annotation { "Feature Type Name" : "Feature", "Feature Type Description" : "" }
export const myFeature = defineFeature(function(context is Context, id is Id, definition is map)
    precondition{}
    {
        {
            var Q0;
            Q0=qCreatedBy(makeId("Right.planeOp"),FACE);
            var sketch = newSketch(context, id + "F0", { "sketchPlane" : qUnion([Q0])});
            skLineSegment(sketch, "E0", {"start": v(0, 0) * mm, "end": v(-381, 0) * mm});
            skLineSegment(sketch, "E1", {"start": v(0, 0) * mm, "end": v(381, 0) * mm});
            skLineSegment(sketch, "E2", {"start": v(0, 0) * mm, "end": v(0, 190.5) * mm});
            skLineSegment(sketch, "E3", {"start": v(-381, 0) * mm, "end": v(0, 190.5) * mm});
            skLineSegment(sketch, "E4", {"start": v(0, 190.5) * mm, "end": v(381, 0) * mm});
            skLineSegment(sketch, "E5", {"start": v(381, 0) * mm, "end": v(457.2, 0) * mm});
            skLineSegment(sketch, "E6", {"start": v(0, 190.5) * mm, "end": v(0, 228.6) * mm});
            skLineSegment(sketch, "E7", {"start": v(-381, 0) * mm, "end": v(-457.2, 0) * mm});
            skLineSegment(sketch, "E8", {"start": v(-457.2, 0) * mm, "end": v(0, 228.6) * mm});
            skLineSegment(sketch, "E9", {"start": v(0, 228.6) * mm, "end": v(457.2, 0) * mm});
            skLineSegment(sketch, "E10", {"start": v(-381, 0) * mm, "end": v(-381, -279.4) * mm});
            skLineSegment(sketch, "E11", {"start": v(381, 0) * mm, "end": v(381, -279.4) * mm});
            skLineSegment(sketch, "E12", {"start": v(-381, -279.4) * mm, "end": v(381, -279.4) * mm});
            skLineSegment(sketch, "E13", {"start": v(-381, -279.4) * mm, "end": v(-381, -330.2) * mm});
            skLineSegment(sketch, "E14", {"start": v(381, -279.4) * mm, "end": v(381, -330.2) * mm});
            skLineSegment(sketch, "E15", {"start": v(-381, -330.2) * mm, "end": v(381, -330.2) * mm});
            skLineSegment(sketch, "E16", {"start": v(381, -279.4) * mm, "end": v(762, -279.4) * mm});
            skLineSegment(sketch, "E17", {"start": v(381, -330.2) * mm, "end": v(762, -330.2) * mm});
            skLineSegment(sketch, "E18", {"start": v(762, -279.4) * mm, "end": v(762, -330.2) * mm});
            skLineSegment(sketch, "E19", {"start": v(762, -279.4) * mm, "end": v(762, -50.8) * mm});
            skLineSegment(sketch, "E20", {"start": v(381, 0) * mm, "end": v(762, -50.8) * mm});
            skLineSegment(sketch, "E21", {"start": v(762, -50.8) * mm, "end": v(762, -101.6) * mm});
            skLineSegment(sketch, "E22", {"start": v(762, -101.6) * mm, "end": v(381, -50.8) * mm});
            skLineSegment(sketch, "E23", {"start": v(-279.4, -279.4) * mm, "end": v(-279.4, -101.6) * mm});
            skLineSegment(sketch, "E24", {"start": v(-279.4, -101.6) * mm, "end": v(-203.2, -101.6) * mm});
            skLineSegment(sketch, "E25", {"start": v(-203.2, -101.6) * mm, "end": v(-203.2, -279.4) * mm});
            skLineSegment(sketch, "E26", {"start": v(-203.2, -279.4) * mm, "end": v(-279.4, -279.4) * mm});
            skLineSegment(sketch, "E27.0", {"start": v(-177.8, -76.2) * mm, "end": v(-177.8, -279.4) * mm});
            skLineSegment(sketch, "E27.1", {"start": v(-304.8, -76.2) * mm, "end": v(-177.8, -76.2) * mm});
            skLineSegment(sketch, "E27.2", {"start": v(-304.8, -279.4) * mm, "end": v(-304.8, -76.2) * mm});
            skLineSegment(sketch, "E28", {"start": v(279.4, -88.9) * mm, "end": v(279.4, -203.2) * mm});
            skLineSegment(sketch, "E29", {"start": v(279.4, -88.9) * mm, "end": v(50.8, -88.9) * mm});
            skLineSegment(sketch, "E30", {"start": v(50.8, -88.9) * mm, "end": v(50.8, -203.2) * mm});
            skLineSegment(sketch, "E31", {"start": v(50.8, -203.2) * mm, "end": v(279.4, -203.2) * mm});
            skLineSegment(sketch, "E32.0", {"start": v(63.5, -101.6) * mm, "end": v(63.5, -190.5) * mm});
            skLineSegment(sketch, "E32.1", {"start": v(266.7, -101.6) * mm, "end": v(63.5, -101.6) * mm});
            skLineSegment(sketch, "E32.2", {"start": v(266.7, -101.6) * mm, "end": v(266.7, -190.5) * mm});
            skLineSegment(sketch, "E32.3", {"start": v(63.5, -190.5) * mm, "end": v(266.7, -190.5) * mm});
            skLineSegment(sketch, "E33.bottom", {"start": v(508, -118.98) * mm, "end": v(609.6, -118.98) * mm});
            skLineSegment(sketch, "E33.top", {"start": v(508, -220.58) * mm, "end": v(609.6, -220.58) * mm});
            skLineSegment(sketch, "E33.left", {"start": v(508, -118.98) * mm, "end": v(508, -220.58) * mm});
            skLineSegment(sketch, "E33.right", {"start": v(609.6, -118.98) * mm, "end": v(609.6, -220.58) * mm});
            skLineSegment(sketch, "E34.0", {"start": v(490.22, -238.36) * mm, "end": v(627.38, -238.36) * mm});
            skLineSegment(sketch, "E34.1", {"start": v(490.22, -101.2) * mm, "end": v(490.22, -238.36) * mm});
            skLineSegment(sketch, "E34.2", {"start": v(490.22, -101.2) * mm, "end": v(627.38, -101.2) * mm});
            skLineSegment(sketch, "E34.3", {"start": v(627.38, -101.2) * mm, "end": v(627.38, -238.36) * mm});
            skSolve(sketch);
        }
        {
            var Q0;
            Q0=makeQuery(id+"F0.imprint","IMPRINT",FACE,{"disambiguationData":[TD([[makeQuery(id+"F0.imprint","IMPRINT",EDGE,{"derivedFrom":sQuery(id+"F0.wireOp",EDGE,"E0")}),1.0]])]});
            var Q1;
            {var subQ5=sQuery(id+"F0.wireOp",EDGE,"E13");Q1=makeQuery(id+"F0.imprint","IMPRINT",FACE,{"disambiguationData":[TD([[makeQuery(id+"F0.imprint","IMPRINT",EDGE,{"derivedFrom":subQ5}),1.0]])]});}
            var Q2;
            Q2=makeQuery(id+"F0.imprint","IMPRINT",FACE,{"disambiguationData":[TD([[makeQuery(id+"F0.imprint","IMPRINT",EDGE,{"derivedFrom":sQuery(id+"F0.wireOp",EDGE,"E14")}),1.0]])]});
            var Q3;
            {var subQ1=sQuery(id+"F0.wireOp",EDGE,"E16");Q3=makeQuery(id+"F0.imprint","IMPRINT",FACE,{"disambiguationData":[TD([[makeQuery(id+"F0.imprint","IMPRINT",EDGE,{"derivedFrom":subQ1}),1.0]])]});}
            var Q4;
            {var subQ0=sQuery(id+"F0.wireOp",EDGE,"E20");Q4=makeQuery(id+"F0.imprint","IMPRINT",FACE,{"disambiguationData":[TD([[makeQuery(id+"F0.imprint","IMPRINT",EDGE,{"derivedFrom":subQ0}),-1.0]])]});}
            var Q5;
            Q5=makeQuery(id+"F0.imprint","IMPRINT",FACE,{"disambiguationData":[TD([[makeQuery(id+"F0.imprint","IMPRINT",EDGE,{"derivedFrom":sQuery(id+"F0.wireOp",EDGE,"E4")}),1.0]])]});
            var Q6;
            Q6=makeQuery(id+"F0.imprint","IMPRINT",FACE,{"disambiguationData":[TD([[makeQuery(id+"F0.imprint","IMPRINT",EDGE,{"derivedFrom":sQuery(id+"F0.wireOp",EDGE,"E1")}),1.0]])]});
            var Q7;
            Q7=makeQuery(id+"F0.imprint","IMPRINT",FACE,{"disambiguationData":[TD([[makeQuery(id+"F0.imprint","IMPRINT",EDGE,{"derivedFrom":sQuery(id+"F0.wireOp",EDGE,"E0")}),-1.0]])]});
            var Q8;
            Q8=makeQuery(id+"F0.imprint","IMPRINT",FACE,{"disambiguationData":[TD([[makeQuery(id+"F0.imprint","IMPRINT",EDGE,{"derivedFrom":sQuery(id+"F0.wireOp",EDGE,"E3")}),1.0]])]});
            extrude(context, id + "F1", {"entities" : qUnion([Q0, Q1, Q2, Q3, Q4, Q5, Q6, Q7, Q8]), "depth" : 688.34 * mm, "offsetDistance" : 25.4 * mm});
        }
        {
            var Q0;
            {var subQ0=sQuery(id+"F0.wireOp",EDGE,"E23");Q0=makeQuery(id+"F0.imprint","IMPRINT",FACE,{"disambiguationData":[TD([[makeQuery(id+"F0.imprint","IMPRINT",EDGE,{"derivedFrom":subQ0}),1.0]])]});}
            var Q1;
            Q1=makeQuery(id+"F0.imprint","IMPRINT",FACE,{"disambiguationData":[TD([[makeQuery(id+"F0.imprint","IMPRINT",EDGE,{"derivedFrom":sQuery(id+"F0.wireOp",EDGE,"E28")}),-1.0]])]});
            var Q2;
            Q2=makeQuery(id+"F0.imprint","IMPRINT",FACE,{"disambiguationData":[TD([[makeQuery(id+"F0.imprint","IMPRINT",EDGE,{"derivedFrom":sQuery(id+"F0.wireOp",EDGE,"E33.bottom")}),1.0]])]});
            extrude(context, id + "F2", {"entities" : qUnion([Q0, Q1, Q2]), "operationType" : NewBodyOperationType.ADD, "depth" : 706.12 * mm, "offsetDistance" : 25.4 * mm});
        }
        {
            var Q0;
            {var subQ5=sQuery(id+"F0.wireOp",EDGE,"E13");Q0=makeQuery(id+"F0.imprint","IMPRINT",FACE,{"disambiguationData":[TD([[makeQuery(id+"F0.imprint","IMPRINT",EDGE,{"derivedFrom":subQ5}),1.0]])]});}
            var Q1;
            Q1=makeQuery(id+"F0.imprint","IMPRINT",FACE,{"disambiguationData":[TD([[makeQuery(id+"F0.imprint","IMPRINT",EDGE,{"derivedFrom":sQuery(id+"F0.wireOp",EDGE,"E14")}),1.0]])]});
            extrude(context, id + "F3", {"entities" : qUnion([Q0, Q1]), "operationType" : NewBodyOperationType.ADD, "oppositeDirection" : true, "depth" : 124.46 * mm, "offsetDistance" : 25.4 * mm});
        }
        {
            var Q0;
            Q0=makeQuery(id+"F0.imprint","IMPRINT",FACE,{"disambiguationData":[TD([[makeQuery(id+"F0.imprint","IMPRINT",EDGE,{"derivedFrom":sQuery(id+"F0.wireOp",EDGE,"E1")}),1.0]])]});
            var sketch = newSketch(context, id + "F4", { "sketchPlane" : qUnion([Q0])});
            skText(sketch, "E35", { "text": "Chloe White\n", "fontName": "OpenSans-Regular.ttf"});
            const initialGuessF4  = {"E35": [-0.75618, 0.59844, 1, 0, 0.25834]};
            skSetInitialGuess(sketch, initialGuessF4);
            skSolve(sketch);
        }
        {
            var Q0;
            Q0=makeQuery(id+"F4.imprint","IMPRINT",FACE,{"disambiguationData":[TD([[makeQuery(id+"F4.imprint","IMPRINT",EDGE,{"derivedFrom":sQuery(id+"F4.wireOp",EDGE,"E35.sketch_text.stroke-73")}),-1.0]])]});
            var Q1;
            Q1=makeQuery(id+"F4.imprint","IMPRINT",FACE,{"disambiguationData":[TD([[makeQuery(id+"F4.imprint","IMPRINT",EDGE,{"derivedFrom":sQuery(id+"F4.wireOp",EDGE,"E35.sketch_text.stroke-54")}),-1.0]])]});
            var Q2;
            Q2=makeQuery(id+"F4.imprint","IMPRINT",FACE,{"disambiguationData":[TD([[makeQuery(id+"F4.imprint","IMPRINT",EDGE,{"derivedFrom":sQuery(id+"F4.wireOp",EDGE,"E35.sketch_text.stroke-37")}),-1.0]])]});
            var Q3;
            Q3=makeQuery(id+"F4.imprint","IMPRINT",FACE,{"disambiguationData":[TD([[makeQuery(id+"F4.imprint","IMPRINT",EDGE,{"derivedFrom":sQuery(id+"F4.wireOp",EDGE,"E35.sketch_text.stroke-33")}),-1.0]])]});
            var Q4;
            Q4=makeQuery(id+"F4.imprint","IMPRINT",FACE,{"disambiguationData":[TD([[makeQuery(id+"F4.imprint","IMPRINT",EDGE,{"derivedFrom":sQuery(id+"F4.wireOp",EDGE,"E35.sketch_text.stroke-93")}),-1.0]])]});
            var Q5;
            Q5=makeQuery(id+"F4.imprint","IMPRINT",FACE,{"disambiguationData":[TD([[makeQuery(id+"F4.imprint","IMPRINT",EDGE,{"derivedFrom":sQuery(id+"F4.wireOp",EDGE,"E35.sketch_text.stroke-111")}),-1.0]])]});
            var Q6;
            Q6=makeQuery(id+"F4.imprint","IMPRINT",FACE,{"disambiguationData":[TD([[makeQuery(id+"F4.imprint","IMPRINT",EDGE,{"derivedFrom":sQuery(id+"F4.wireOp",EDGE,"E35.sketch_text.stroke-115")}),-1.0]])]});
            var Q7;
            Q7=makeQuery(id+"F4.imprint","IMPRINT",FACE,{"disambiguationData":[TD([[makeQuery(id+"F4.imprint","IMPRINT",EDGE,{"derivedFrom":sQuery(id+"F4.wireOp",EDGE,"E35.sketch_text.stroke-123")}),-1.0]])]});
            var Q8;
            Q8=makeQuery(id+"F4.imprint","IMPRINT",FACE,{"disambiguationData":[TD([[makeQuery(id+"F4.imprint","IMPRINT",EDGE,{"derivedFrom":sQuery(id+"F4.wireOp",EDGE,"E35.sketch_text.stroke-142")}),-1.0]])]});
            var Q9;
            Q9=makeQuery(id+"F4.imprint","IMPRINT",FACE,{"disambiguationData":[TD([[makeQuery(id+"F4.imprint","IMPRINT",EDGE,{"derivedFrom":sQuery(id+"F4.wireOp",EDGE,"E35.sketch_text.stroke-15")}),-1.0]])]});
            var Q10;
            Q10=makeQuery(id+"F4.imprint","IMPRINT",FACE,{"disambiguationData":[TD([[makeQuery(id+"F4.imprint","IMPRINT",EDGE,{"derivedFrom":sQuery(id+"F4.wireOp",EDGE,"E35.sketch_text.stroke-0")}),-1.0]])]});
            extrude(context, id + "F5", {"entities" : qUnion([Q0, Q1, Q2, Q3, Q4, Q5, Q6, Q7, Q8, Q9, Q10]), "depth" : 53.34 * mm, "offsetDistance" : 25.4 * mm});
        }
    });